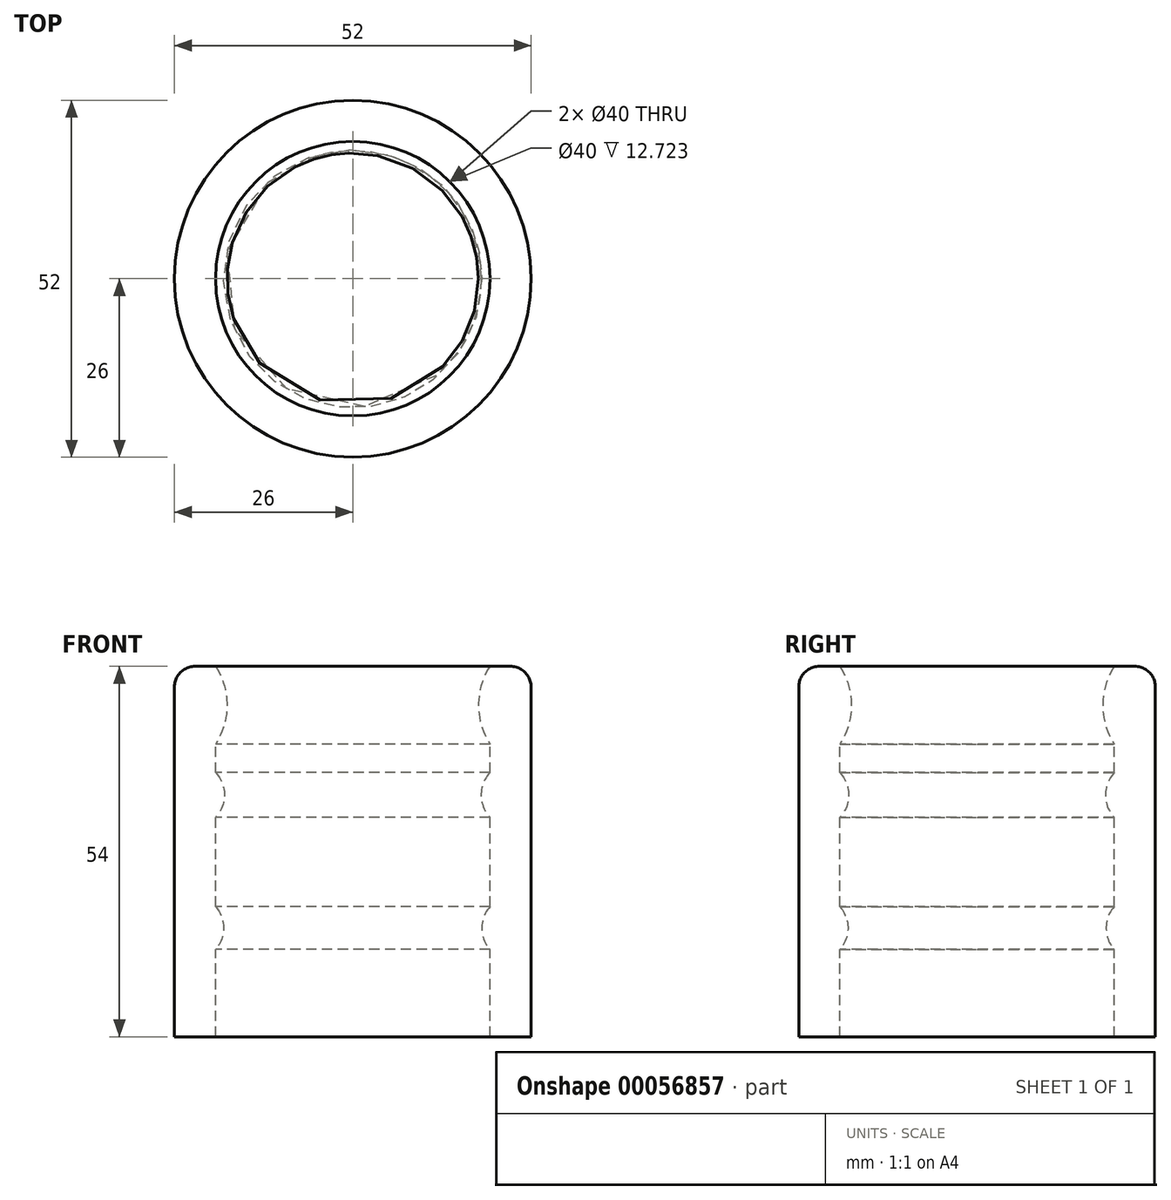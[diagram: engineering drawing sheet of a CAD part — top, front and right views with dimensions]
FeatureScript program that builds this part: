
annotation { "Feature Type Name" : "Feature", "Feature Type Description" : "" }
export const myFeature = defineFeature(function(context is Context, id is Id, definition is map)
    precondition{}
    {
        {
            var Q0;
            Q0=qCreatedBy(makeId("Front.planeOp"),FACE);
            var sketch = newSketch(context, id + "F0", { "sketchPlane" : qUnion([Q0])});
            skLineSegment(sketch, "E0", {"start": v(0, 38.83) * mm, "end": v(0, -7.78) * mm, "construction": true});
            skLineSegment(sketch, "E1.0", {"start": v(-20, 52.66) * mm, "end": v(-20, 48.5) * mm, "construction": true});
            skLineSegment(sketch, "E2", {"start": v(-13.36, 0) * mm, "end": v(11.25, 0) * mm, "construction": true});
            skLineSegment(sketch, "E3.0", {"start": v(-13.36, 10) * mm, "end": v(11.25, 10) * mm, "construction": true});
            skLineSegment(sketch, "E4.0", {"start": v(-13.36, 64) * mm, "end": v(11.25, 64) * mm, "construction": true});
            skLineSegment(sketch, "E5.trimOffspring", {"start": v(-20, 0) * mm, "end": v(-20, -7.78) * mm, "construction": true});
            skLineSegment(sketch, "E6.0", {"start": v(-26, 64) * mm, "end": v(-26, 10) * mm, "construction": true});
            skLineSegment(sketch, "E7", {"start": v(-20, 64) * mm, "end": v(-26, 64) * mm});
            skLineSegment(sketch, "E8", {"start": v(-26, 10) * mm, "end": v(-20, 10) * mm});
            skLineSegment(sketch, "E9", {"start": v(-20, 52.66) * mm, "end": v(-20, 48.5) * mm});
            skLineSegment(sketch, "E10", {"start": v(-26, 10) * mm, "end": v(-26, 64) * mm});
            skLineSegment(sketch, "E11.0", {"start": v(12, 38.83) * mm, "end": v(12, -7.78) * mm, "construction": true});
            skLineSegment(sketch, "E12.0", {"start": v(-13.36, -5) * mm, "end": v(11.25, -5) * mm, "construction": true});
            skLineSegment(sketch, "E13", {"start": v(12, -5) * mm, "end": v(17.08, -5) * mm});
            skLineSegment(sketch, "E14.0", {"start": v(12, -9) * mm, "end": v(17.08, -9) * mm});
            skLineSegment(sketch, "E15", {"start": v(12, -5) * mm, "end": v(12, -9) * mm});
            skLineSegment(sketch, "E16.0", {"start": v(16, -5) * mm, "end": v(16, -9) * mm});
            skArc(sketch, "E17", {"start": v(0, 10) * mm, "mid": v(5.02, 3.82) * mm, "end": v(12, 0) * mm});
            skLineSegment(sketch, "E18", {"start": v(0, 10) * mm, "end": v(23.54, -2.98) * mm});
            skArc(sketch, "E19", {"start": v(0, 10) * mm, "mid": v(9.8, -0.05) * mm, "end": v(23.54, -2.98) * mm});
            skArc(sketch, "E20", {"start": v(-20, 22.72) * mm, "mid": v(-18.82, 25.84) * mm, "end": v(-20, 28.96) * mm});
            skArc(sketch, "E21", {"start": v(-20, 41.98) * mm, "mid": v(-18.71, 45.24) * mm, "end": v(-20, 48.5) * mm});
            skArc(sketch, "E22", {"start": v(-20, 52.66) * mm, "mid": v(-18.33, 58.33) * mm, "end": v(-20, 64) * mm});
            skLineSegment(sketch, "E23.trimOffspring", {"start": v(-20, 41.98) * mm, "end": v(-20, 28.96) * mm, "construction": true});
            skLineSegment(sketch, "E24.trimOffspring", {"start": v(-20, 22.72) * mm, "end": v(-20, 10) * mm, "construction": true});
            skLineSegment(sketch, "E25.trimOffspring", {"start": v(-20, 41.98) * mm, "end": v(-20, 28.96) * mm});
            skLineSegment(sketch, "E26.trimOffspring", {"start": v(-20, 22.72) * mm, "end": v(-20, 10) * mm});
            skSolve(sketch);
        }
        {
            var Q0;
            Q0=makeQuery(id+"F0.imprint","IMPRINT",FACE,{"disambiguationData":[TD([[makeQuery(id+"F0.imprint","IMPRINT",EDGE,{"derivedFrom":sQuery(id+"F0.wireOp",EDGE,"E7")}),1.0]])]});
            var Q1;
            Q1=sQuery(id+"F0.wireOp",EDGE,"E0");
            revolve(context, id + "F1", {"entities" : qUnion([Q0]), "axis" : qUnion([Q1]), "revolveType" : RevolveType.FULL});
        }
        {
            var Q0;
            Q0=makeQuery(id+"F1.opRevolve","SWEPT_EDGE",EDGE,{"disambiguationData":[OSD([sQuery(id+"F0.wireOp",EDGE,"E7"),sQuery(id+"F0.wireOp",EDGE,"E10")])]});
            fillet(context, id + "F2", {"entities" : qUnion([Q0]), "radius" : 3 * mm, "tangentPropagation" : true, "allowEdgeOverflow" : false});
        }
    });
